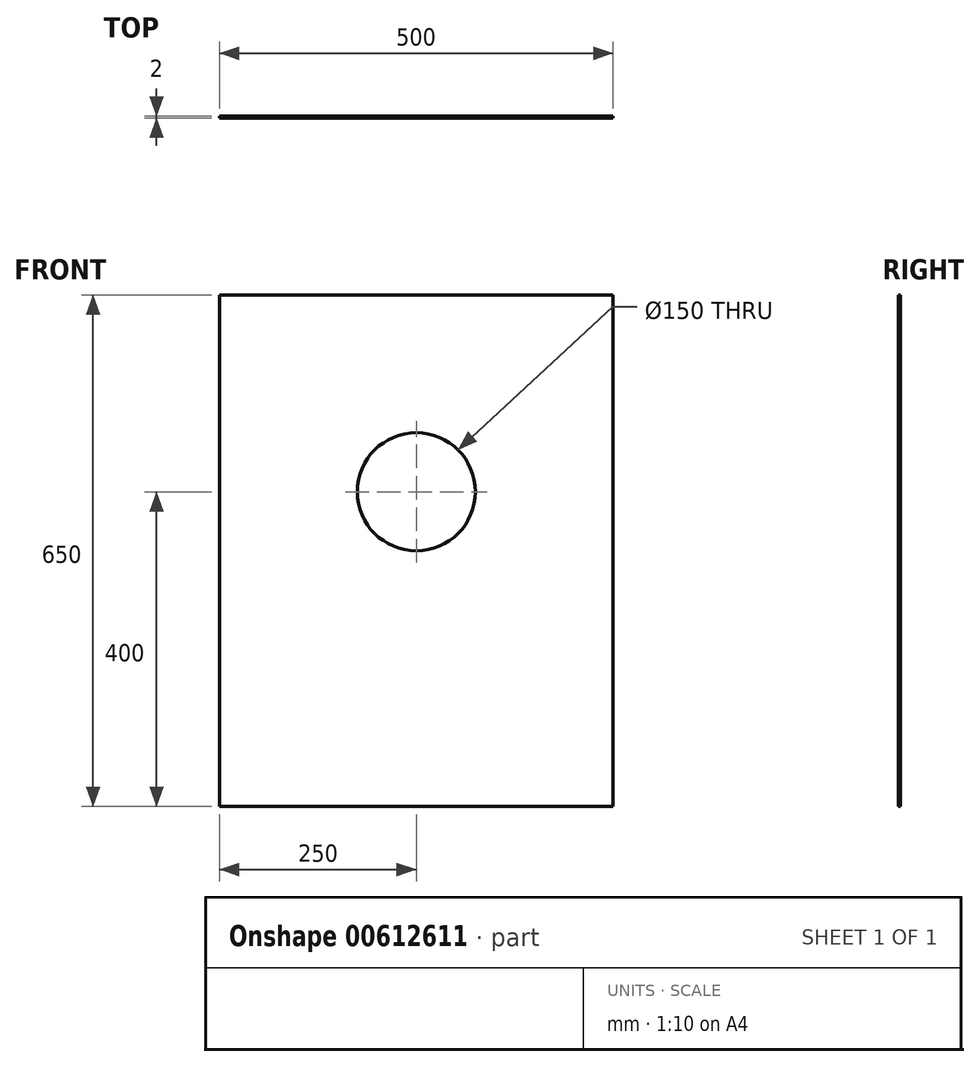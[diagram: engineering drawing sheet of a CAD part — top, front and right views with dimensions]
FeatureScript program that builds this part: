
annotation { "Feature Type Name" : "Feature", "Feature Type Description" : "" }
export const myFeature = defineFeature(function(context is Context, id is Id, definition is map)
    precondition{}
    {
        {
            var Q0;
            Q0=qCreatedBy(makeId("Front.planeOp"),FACE);
            var sketch = newSketch(context, id + "F0", { "sketchPlane" : qUnion([Q0])});
            skLineSegment(sketch, "E0.bottom", {"start": v(-250, 325) * mm, "end": v(250, 325) * mm});
            skLineSegment(sketch, "E0.top", {"start": v(-250, -325) * mm, "end": v(250, -325) * mm});
            skLineSegment(sketch, "E0.left", {"start": v(-250, 325) * mm, "end": v(-250, -325) * mm});
            skLineSegment(sketch, "E0.right", {"start": v(250, 325) * mm, "end": v(250, -325) * mm});
            skPoint(sketch, "E0.middle", {"position": v(0, 0) * mm});
            skCircle(sketch, "E1", {"center": v(0, 75) * mm, "radius": 75 * mm});
            skSolve(sketch);
        }
        {
            var Q0;
            Q0=makeQuery(id+"F0.imprint","IMPRINT",FACE,{"disambiguationData":[TD([[makeQuery(id+"F0.imprint","IMPRINT",EDGE,{"derivedFrom":sQuery(id+"F0.wireOp",EDGE,"E0.bottom")}),-1.0]])]});
            extrude(context, id + "F1", {"entities" : qUnion([Q0]), "depth" : 2 * mm, "offsetDistance" : 25.4 * mm});
        }
    });
